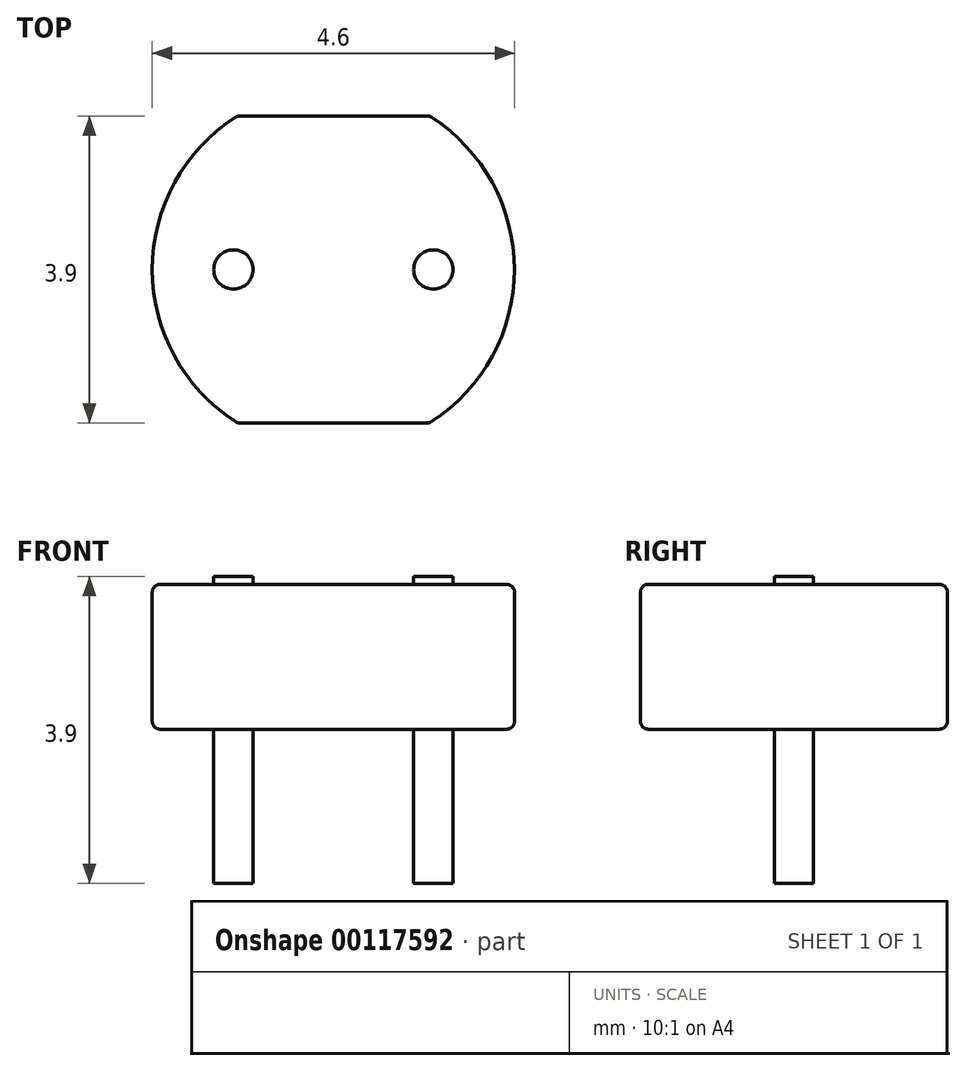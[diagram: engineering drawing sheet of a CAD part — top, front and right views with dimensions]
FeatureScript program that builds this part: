
annotation { "Feature Type Name" : "Feature", "Feature Type Description" : "" }
export const myFeature = defineFeature(function(context is Context, id is Id, definition is map)
    precondition{}
    {
        {
            var Q0;
            Q0=qCreatedBy(makeId("Top.planeOp"),FACE);
            var sketch = newSketch(context, id + "F0", { "sketchPlane" : qUnion([Q0])});
            skArc(sketch, "E0", {"start": v(-1.22, 1.95) * mm, "mid": v(-2.3, 0) * mm, "end": v(-1.22, -1.95) * mm});
            skLineSegment(sketch, "E1", {"start": v(-1.22, 1.95) * mm, "end": v(1.22, 1.95) * mm});
            skLineSegment(sketch, "E2", {"start": v(-1.22, -1.95) * mm, "end": v(1.22, -1.95) * mm});
            skLineSegment(sketch, "E3", {"start": v(2.3, 0) * mm, "end": v(-2.3, 0) * mm, "construction": true});
            skArc(sketch, "E4.trimOffspring", {"start": v(1.22, -1.95) * mm, "mid": v(2.3, 0) * mm, "end": v(1.22, 1.95) * mm});
            skSolve(sketch);
        }
        {
            var Q0;
            Q0 = qSketchRegion(id + "F0", true);
            var Q1;
            Q1=makeQuery(id+"F0.imprint","IMPRINT",FACE,{"disambiguationData":[TD([[makeQuery(id+"F0.imprint","IMPRINT",EDGE,{"derivedFrom":sQuery(id+"F0.wireOp",EDGE,"E0")}),1.0]])]});
            extrude(context, id + "F1", {"entities" : qUnion([Q0, Q1]), "depth" : 1.84 * mm});
        }
        {
            var Q0;
            Q0=makeQuery(id+"F1.opExtrude","CAP_EDGE",EDGE,{"disambiguationData":[OSD([sQuery(id+"F0.wireOp",EDGE,"E1")])],"isStart":false});
            var Q1;
            Q1=makeQuery(id+"F1.opExtrude","CAP_EDGE",EDGE,{"disambiguationData":[OSD([sQuery(id+"F0.wireOp",EDGE,"E0")])],"isStart":false});
            var Q2;
            Q2=makeQuery(id+"F1.opExtrude","CAP_EDGE",EDGE,{"disambiguationData":[OSD([sQuery(id+"F0.wireOp",EDGE,"E2")])],"isStart":false});
            var Q3;
            Q3=makeQuery(id+"F1.opExtrude","CAP_EDGE",EDGE,{"disambiguationData":[OSD([sQuery(id+"F0.wireOp",EDGE,"E4.trimOffspring")])],"isStart":false});
            var Q4;
            Q4=makeQuery(id+"F1.opExtrude","SWEPT_EDGE",EDGE,{"disambiguationData":[OSD([sQuery(id+"F0.wireOp",EDGE,"E0"),sQuery(id+"F0.wireOp",EDGE,"E1")])]});
            var Q5;
            Q5=makeQuery(id+"F1.opExtrude","SWEPT_EDGE",EDGE,{"disambiguationData":[OSD([sQuery(id+"F0.wireOp",EDGE,"E1"),sQuery(id+"F0.wireOp",EDGE,"E4.trimOffspring")])]});
            var Q6;
            Q6=makeQuery(id+"F1.opExtrude","CAP_EDGE",EDGE,{"disambiguationData":[OSD([sQuery(id+"F0.wireOp",EDGE,"E1")])],"isStart":true});
            var Q7;
            Q7=makeQuery(id+"F1.opExtrude","CAP_EDGE",EDGE,{"disambiguationData":[OSD([sQuery(id+"F0.wireOp",EDGE,"E0")])],"isStart":true});
            var Q8;
            Q8=makeQuery(id+"F1.opExtrude","SWEPT_EDGE",EDGE,{"disambiguationData":[OSD([sQuery(id+"F0.wireOp",EDGE,"E0"),sQuery(id+"F0.wireOp",EDGE,"E2")])]});
            var Q9;
            Q9=makeQuery(id+"F1.opExtrude","SWEPT_EDGE",EDGE,{"disambiguationData":[OSD([sQuery(id+"F0.wireOp",EDGE,"E2"),sQuery(id+"F0.wireOp",EDGE,"E4.trimOffspring")])]});
            var Q10;
            Q10=makeQuery(id+"F1.opExtrude","CAP_EDGE",EDGE,{"disambiguationData":[OSD([sQuery(id+"F0.wireOp",EDGE,"E4.trimOffspring")])],"isStart":true});
            var Q11;
            Q11=makeQuery(id+"F1.opExtrude","CAP_EDGE",EDGE,{"disambiguationData":[OSD([sQuery(id+"F0.wireOp",EDGE,"E2")])],"isStart":true});
            fillet(context, id + "F2", {"entities" : qUnion([Q0, Q1, Q2, Q3, Q4, Q5, Q6, Q7, Q8, Q9, Q10, Q11]), "radius" : 0.1 * mm, "tangentPropagation" : true, "allowEdgeOverflow" : false});
        }
        {
            var Q0;
            Q0=makeQuery(id+"F1.opExtrude","CAP_FACE",FACE,{"disambiguationData":[OSD([sQuery(id+"F0.wireOp",EDGE,"E0"),sQuery(id+"F0.wireOp",EDGE,"E1"),sQuery(id+"F0.wireOp",EDGE,"E2"),sQuery(id+"F0.wireOp",EDGE,"E4.trimOffspring")])],"isStart":false});
            var sketch = newSketch(context, id + "F3", { "sketchPlane" : qUnion([Q0])});
            skLineSegment(sketch, "E5", {"start": v(0, 1.85) * mm, "end": v(0, -1.85) * mm, "construction": true});
            skCircle(sketch, "E6", {"center": v(-1.27, 0) * mm, "radius": 0.25 * mm});
            skCircle(sketch, "E7.MirrorC", {"center": v(1.27, 0) * mm, "radius": 0.25 * mm});
            skSolve(sketch);
        }
        {
            var Q0;
            Q0 = qSketchRegion(id + "F3", true);
            extrude(context, id + "F4", {"entities" : qUnion([Q0]), "operationType" : NewBodyOperationType.ADD, "depth" : 0.1 * mm, "hasSecondDirection" : true, "secondDirectionOppositeDirection" : true, "secondDirectionDepth" : 3.8 * mm});
        }
    });
